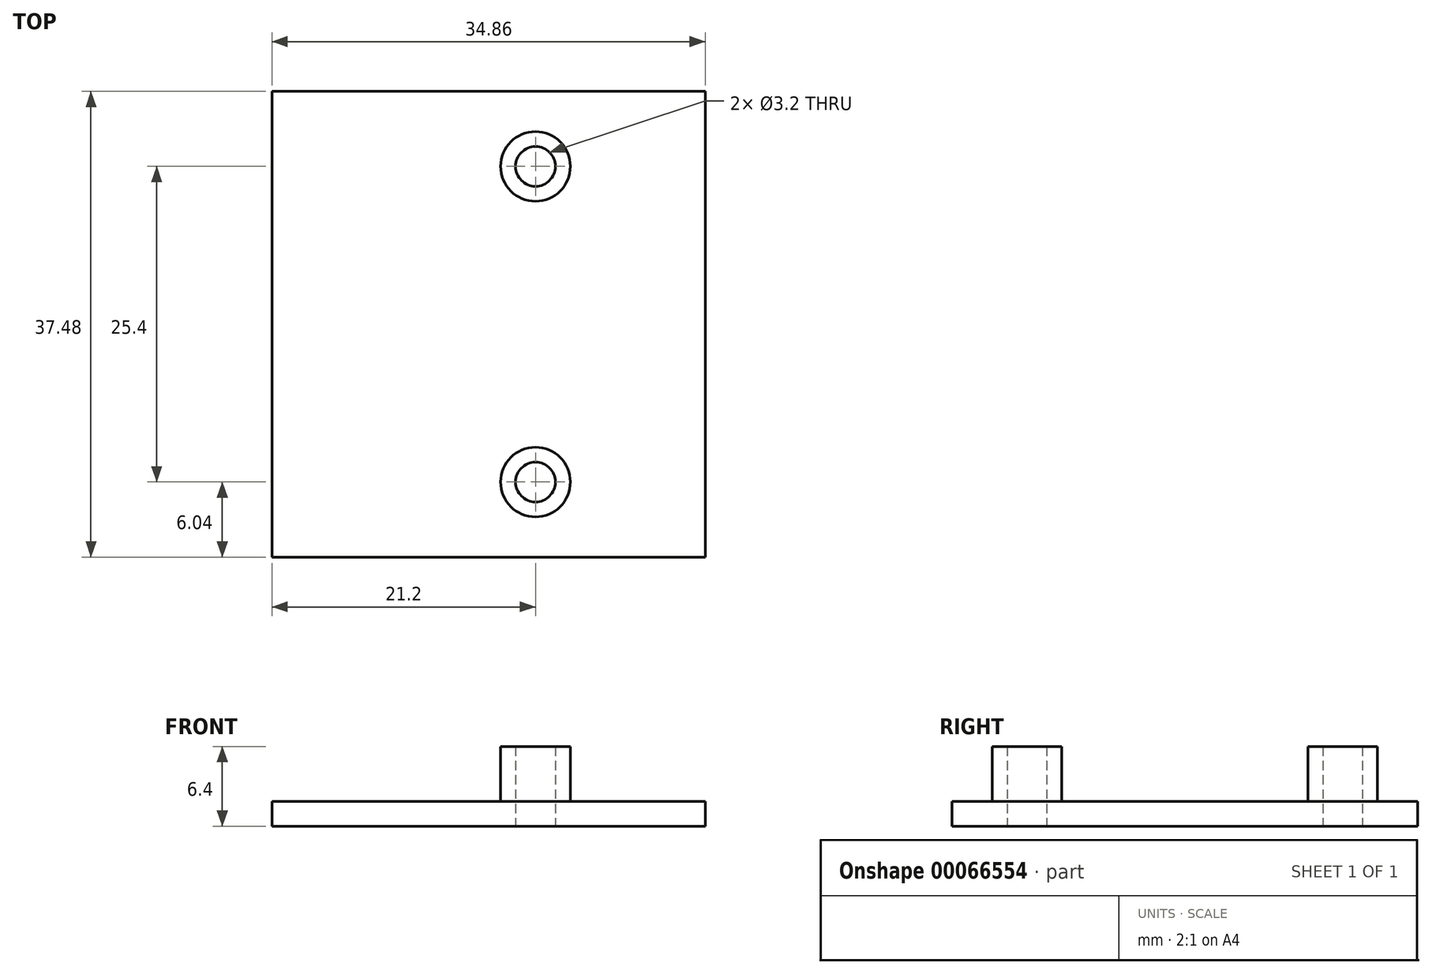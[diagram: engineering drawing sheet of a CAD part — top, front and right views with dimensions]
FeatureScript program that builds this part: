
annotation { "Feature Type Name" : "Feature", "Feature Type Description" : "" }
export const myFeature = defineFeature(function(context is Context, id is Id, definition is map)
    precondition{}
    {
        {
            var Q0;
            Q0=qCreatedBy(makeId("Top.planeOp"),FACE);
            var sketch = newSketch(context, id + "F0", { "sketchPlane" : qUnion([Q0])});
            skLineSegment(sketch, "E0.rect.bottom", {"start": v(14.03, -15.33) * mm, "end": v(-14.03, -15.34) * mm, "construction": true});
            skLineSegment(sketch, "E0.rect.top", {"start": v(14.03, 15.34) * mm, "end": v(-14.03, 15.33) * mm, "construction": true});
            skLineSegment(sketch, "E0.rect.left", {"start": v(14.03, -15.33) * mm, "end": v(14.03, 15.34) * mm, "construction": true});
            skLineSegment(sketch, "E0.rect.right", {"start": v(-14.03, -15.34) * mm, "end": v(-14.03, 15.34) * mm, "construction": true});
            skPoint(sketch, "E0.rect.middle", {"position": v(0, 0) * mm});
            skCircle(sketch, "E1", {"center": v(3.77, 12.7) * mm, "radius": 1.6 * mm});
            skCircle(sketch, "E2", {"center": v(3.77, -12.7) * mm, "radius": 1.6 * mm});
            skPoint(sketch, "E3", {"position": v(3.77, 14.3) * mm});
            skPoint(sketch, "E4", {"position": v(3.77, -11.1) * mm});
            skPoint(sketch, "E5", {"position": v(3.77, -14.3) * mm});
            skPoint(sketch, "E6", {"position": v(3.77, 11.1) * mm});
            skLineSegment(sketch, "E7.rect.bottom", {"start": v(15.03, -16.33) * mm, "end": v(-15.03, -16.34) * mm});
            skLineSegment(sketch, "E7.rect.top", {"start": v(15.03, 16.34) * mm, "end": v(-15.03, 16.33) * mm});
            skLineSegment(sketch, "E7.rect.left", {"start": v(15.03, -16.33) * mm, "end": v(15.03, 16.34) * mm});
            skLineSegment(sketch, "E7.rect.right", {"start": v(-15.03, -16.33) * mm, "end": v(-15.03, 16.34) * mm});
            skLineSegment(sketch, "E8.rect.bottom", {"start": v(17.43, -18.73) * mm, "end": v(-17.43, -18.74) * mm});
            skLineSegment(sketch, "E8.rect.top", {"start": v(17.43, 18.74) * mm, "end": v(-17.43, 18.73) * mm});
            skLineSegment(sketch, "E8.rect.left", {"start": v(17.43, -18.74) * mm, "end": v(17.43, 18.74) * mm});
            skLineSegment(sketch, "E8.rect.right", {"start": v(-17.43, -18.74) * mm, "end": v(-17.43, 18.74) * mm});
            skCircle(sketch, "E9", {"center": v(3.77, 12.7) * mm, "radius": 2.8 * mm});
            skCircle(sketch, "E10", {"center": v(3.77, -12.7) * mm, "radius": 2.8 * mm});
            skLineSegment(sketch, "E11.rect.bottom", {"start": v(12.47, 6.84) * mm, "end": v(9.97, 6.84) * mm, "construction": true});
            skLineSegment(sketch, "E11.rect.top", {"start": v(12.47, 11.54) * mm, "end": v(9.97, 11.53) * mm, "construction": true});
            skLineSegment(sketch, "E11.rect.left", {"start": v(12.47, 6.84) * mm, "end": v(12.47, 11.54) * mm, "construction": true});
            skLineSegment(sketch, "E11.rect.right", {"start": v(9.97, 6.84) * mm, "end": v(9.97, 11.54) * mm, "construction": true});
            skPoint(sketch, "E11.rect.middle", {"position": v(11.22, 9.19) * mm});
            skLineSegment(sketch, "E12.rect.bottom", {"start": v(12.47, -2.11) * mm, "end": v(9.97, -2.11) * mm, "construction": true});
            skLineSegment(sketch, "E12.rect.top", {"start": v(12.47, 2.59) * mm, "end": v(9.97, 2.58) * mm, "construction": true});
            skLineSegment(sketch, "E12.rect.left", {"start": v(12.47, -2.11) * mm, "end": v(12.47, 2.59) * mm, "construction": true});
            skLineSegment(sketch, "E12.rect.right", {"start": v(9.97, -2.11) * mm, "end": v(9.97, 2.59) * mm, "construction": true});
            skPoint(sketch, "E12.rect.middle", {"position": v(11.22, 0.24) * mm});
            skLineSegment(sketch, "E13.rect.bottom", {"start": v(12.47, -6.43) * mm, "end": v(9.97, -6.43) * mm, "construction": true});
            skLineSegment(sketch, "E13.rect.top", {"start": v(12.47, -11.13) * mm, "end": v(9.97, -11.13) * mm, "construction": true});
            skLineSegment(sketch, "E13.rect.left", {"start": v(12.47, -6.43) * mm, "end": v(12.47, -11.13) * mm, "construction": true});
            skLineSegment(sketch, "E13.rect.right", {"start": v(9.97, -6.43) * mm, "end": v(9.97, -11.13) * mm, "construction": true});
            skPoint(sketch, "E13.rect.middle", {"position": v(11.22, -8.79) * mm});
            skPoint(sketch, "E13.rect.middle.positionSnap0", {"position": v(11.22, -2.11) * mm});
            skPoint(sketch, "E13.rect.centerSnap0", {"position": v(11.22, -2.11) * mm});
            skLineSegment(sketch, "E14.rect.bottom", {"start": v(13.47, 5.84) * mm, "end": v(8.97, 5.83) * mm});
            skLineSegment(sketch, "E14.rect.top", {"start": v(13.47, 12.54) * mm, "end": v(8.97, 12.54) * mm});
            skLineSegment(sketch, "E14.rect.left", {"start": v(13.47, 5.84) * mm, "end": v(13.47, 12.54) * mm});
            skLineSegment(sketch, "E14.rect.right", {"start": v(8.97, 5.83) * mm, "end": v(8.97, 12.54) * mm});
            skLineSegment(sketch, "E15.rect.bottom", {"start": v(13.47, 3.59) * mm, "end": v(8.97, 3.59) * mm});
            skLineSegment(sketch, "E15.rect.top", {"start": v(13.47, -3.11) * mm, "end": v(8.97, -3.11) * mm});
            skLineSegment(sketch, "E15.rect.left", {"start": v(13.47, 3.59) * mm, "end": v(13.47, -3.11) * mm});
            skLineSegment(sketch, "E15.rect.right", {"start": v(8.97, 3.59) * mm, "end": v(8.97, -3.11) * mm});
            skLineSegment(sketch, "E16.rect.bottom", {"start": v(13.47, -5.43) * mm, "end": v(8.97, -5.43) * mm});
            skLineSegment(sketch, "E16.rect.top", {"start": v(13.47, -12.13) * mm, "end": v(8.97, -12.13) * mm});
            skLineSegment(sketch, "E16.rect.left", {"start": v(13.47, -5.43) * mm, "end": v(13.47, -12.13) * mm});
            skLineSegment(sketch, "E16.rect.right", {"start": v(8.97, -5.43) * mm, "end": v(8.97, -12.13) * mm});
            skLineSegment(sketch, "E17.rect.bottom", {"start": v(-11.53, -13.06) * mm, "end": v(-14.03, -13.06) * mm, "construction": true});
            skLineSegment(sketch, "E17.rect.top", {"start": v(-11.53, -5.74) * mm, "end": v(-14.03, -5.74) * mm, "construction": true});
            skLineSegment(sketch, "E17.rect.left", {"start": v(-11.53, -13.06) * mm, "end": v(-11.53, -5.74) * mm, "construction": true});
            skLineSegment(sketch, "E17.rect.right", {"start": v(-14.03, -13.06) * mm, "end": v(-14.03, -5.74) * mm, "construction": true});
            skPoint(sketch, "E17.rect.middle", {"position": v(-12.78, -9.4) * mm});
            skLineSegment(sketch, "E18.rect.bottom", {"start": v(-9.03, -4.74) * mm, "end": v(-14.03, -4.74) * mm, "construction": true});
            skLineSegment(sketch, "E18.rect.top", {"start": v(-9.03, 2.56) * mm, "end": v(-14.03, 2.56) * mm, "construction": true});
            skLineSegment(sketch, "E18.rect.left", {"start": v(-9.03, -4.74) * mm, "end": v(-9.03, 2.56) * mm, "construction": true});
            skLineSegment(sketch, "E18.rect.right", {"start": v(-14.03, -4.74) * mm, "end": v(-14.03, 2.56) * mm, "construction": true});
            skPoint(sketch, "E18.rect.middle", {"position": v(-11.53, -1.09) * mm});
            skLineSegment(sketch, "E19", {"start": v(-14.03, -14.06) * mm, "end": v(-10.53, -14.06) * mm});
            skLineSegment(sketch, "E20", {"start": v(-10.53, -14.06) * mm, "end": v(-10.53, -5.74) * mm});
            skLineSegment(sketch, "E21", {"start": v(-10.53, -5.74) * mm, "end": v(-8.03, -5.74) * mm});
            skLineSegment(sketch, "E22", {"start": v(-8.03, -5.74) * mm, "end": v(-8.03, 3.56) * mm});
            skLineSegment(sketch, "E23", {"start": v(-8.03, 3.56) * mm, "end": v(-15.03, 3.56) * mm});
            skLineSegment(sketch, "E24", {"start": v(-15.03, 3.56) * mm, "end": v(-15.03, -14.06) * mm});
            skLineSegment(sketch, "E25", {"start": v(-15.03, -14.06) * mm, "end": v(-14.03, -14.06) * mm});
            skLineSegment(sketch, "E26", {"start": v(0, 5) * mm, "end": v(0, -5) * mm, "construction": true});
            skArc(sketch, "E27.0.startCap", {"start": v(-1.63, 5) * mm, "mid": v(0, 6.63) * mm, "end": v(1.62, 5) * mm, "construction": true});
            skArc(sketch, "E27.0.endCap", {"start": v(1.63, -5) * mm, "mid": v(0, -6.63) * mm, "end": v(-1.62, -5) * mm, "construction": true});
            skLineSegment(sketch, "E27.0.left", {"start": v(1.63, 5) * mm, "end": v(1.63, -5) * mm, "construction": true});
            skLineSegment(sketch, "E27.0.right", {"start": v(-1.63, 5) * mm, "end": v(-1.62, -5) * mm, "construction": true});
            skSolve(sketch);
        }
        {
            var Q0;
            {var subQ1=sQuery(id+"F0.wireOp",EDGE,"E7.rect.bottom");Q0=makeQuery(id+"F0.imprint","IMPRINT",FACE,{"disambiguationData":[TD([[makeQuery(id+"F0.imprint","IMPRINT",EDGE,{"derivedFrom":subQ1}),1.0]])]});}
            var Q1;
            {var subQ2=sQuery(id+"F0.wireOp",EDGE,"E7.rect.bottom");Q1=makeQuery(id+"F0.imprint","IMPRINT",FACE,{"disambiguationData":[TD([[makeQuery(id+"F0.imprint","IMPRINT",EDGE,{"derivedFrom":subQ2}),-1.0]])]});}
            var Q2;
            Q2=makeQuery(id+"F0.imprint","IMPRINT",FACE,{"disambiguationData":[TD([[makeQuery(id+"F0.imprint","IMPRINT",EDGE,{"derivedFrom":sQuery(id+"F0.wireOp",EDGE,"E19")}),1.0]])]});
            var Q3;
            Q3=makeQuery(id+"F0.imprint","IMPRINT",FACE,{"disambiguationData":[TD([[makeQuery(id+"F0.imprint","IMPRINT",EDGE,{"derivedFrom":sQuery(id+"F0.wireOp",EDGE,"E1")}),-1.0]])]});
            var Q4;
            Q4=makeQuery(id+"F0.imprint","IMPRINT",FACE,{"disambiguationData":[TD([[makeQuery(id+"F0.imprint","IMPRINT",EDGE,{"derivedFrom":sQuery(id+"F0.wireOp",EDGE,"E2")}),-1.0]])]});
            var Q5;
            Q5=makeQuery(id+"F0.imprint","IMPRINT",FACE,{"disambiguationData":[TD([[makeQuery(id+"F0.imprint","IMPRINT",EDGE,{"derivedFrom":sQuery(id+"F0.wireOp",EDGE,"E14.rect.bottom")}),-1.0]])]});
            var Q6;
            Q6=makeQuery(id+"F0.imprint","IMPRINT",FACE,{"disambiguationData":[TD([[makeQuery(id+"F0.imprint","IMPRINT",EDGE,{"derivedFrom":sQuery(id+"F0.wireOp",EDGE,"E15.rect.bottom")}),1.0]])]});
            var Q7;
            Q7=makeQuery(id+"F0.imprint","IMPRINT",FACE,{"disambiguationData":[TD([[makeQuery(id+"F0.imprint","IMPRINT",EDGE,{"derivedFrom":sQuery(id+"F0.wireOp",EDGE,"E16.rect.bottom")}),1.0]])]});
            extrude(context, id + "F1", {"entities" : qUnion([Q0, Q1, Q2, Q3, Q4, Q5, Q6, Q7]), "depth" : 2 * mm});
        }
        {
            var Q0;
            Q0=makeQuery(id+"F0.imprint","IMPRINT",FACE,{"disambiguationData":[TD([[makeQuery(id+"F0.imprint","IMPRINT",EDGE,{"derivedFrom":sQuery(id+"F0.wireOp",EDGE,"E1")}),-1.0]])]});
            var Q1;
            Q1=makeQuery(id+"F0.imprint","IMPRINT",FACE,{"disambiguationData":[TD([[makeQuery(id+"F0.imprint","IMPRINT",EDGE,{"derivedFrom":sQuery(id+"F0.wireOp",EDGE,"E2")}),-1.0]])]});
            extrude(context, id + "F2", {"entities" : qUnion([Q0, Q1]), "operationType" : NewBodyOperationType.ADD, "depth" : 6.4 * mm});
        }
    });
